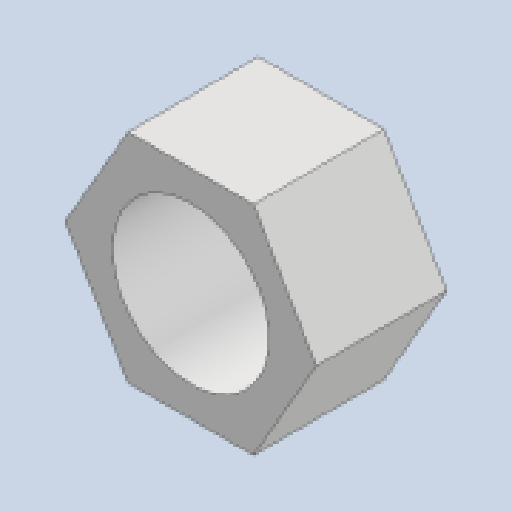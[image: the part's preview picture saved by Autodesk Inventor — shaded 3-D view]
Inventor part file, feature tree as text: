
AUTODESK INVENTOR PART (.ipt)
format: ipt  version: 2023.1 (Build 271208000, 208)  size: 97,792 bytes
history: native  units: mm
features: other x2, extrude x1, sketch x1
ambient origin geometry x8: Origin, YZ Plane, XZ Plane, XY Plane, X Axis, Y Axis, Z Axis, Center Point
bodies: Body1 (feature_tree)
feature tree (4):
  other  "솔리드1"
  extrude  "돌출1"  Depth=6.0mm
  other  "스레드1"
  sketch  "스케치1"
